# Revit family: LRO
name_source: partatom
category: Lighting Fixtures
revit_build: Autodesk Revit MEP 2012 (Build: 20110916_2132(x64)
units: mm (PartAtom-declared; Revit-internal decimal feet)

## types (2) — shared parameters
Apparent Load = 0 VA
Backbox = White
Color Filter = 16777215
Default Elevation = 4.00'
Description = This commercial grade LED lensed strip is available in 4' or 8' lengths, multiple lumen packages from 2,700 to 19,200 nominal, choice of LED color and an optional integral 1400 lumen battery pack.
Dimming Lamp Color Temperature Shift = <None>
Driver = 0-10V Dimming
Emit from Line Length = 1.00'
Glass = White Glass
Lamp = LED Lamp
Manufacturer = Columbia Lighting
Manufacturer Fax = (866)-898-1065
Model = LRO
Product Documentation Link = http://www.columbialighting.com
Product Page URL = http://www.columbialighting.com
Row Length = 4.00'
Tilt Angle = -90.00°
URL = http://www.columbialighting.com
Voltage = 120 V

## per-type parameters (varying)
| type | Lumen Output | Nominal Watts | Photometric Web File |
| LRO4-35ML-EDU | Medium Lumen | 53 W | LRO4-35ML-EDU.ies |
| LRO4-35VL-EDU | Very High Lumen | 105 W | LRO4-35VL-EDU.ies |

## geometry (parser evidence)
native form markers: Sweep x4
no freeform markers — native parametric forms only
